# Revit family: Faucet_Bathroom-DXV-Equility-D3510940X_Series
name_source: partatom
category: Plumbing Fixtures
revit_build: Autodesk Revit 2014 (Build: 20130308_1515(x64)
units: mm (PartAtom-declared; Revit-internal decimal feet)

## types (9) — shared parameters
ADA Compliant = Yes
Assembly Code = D2010710
CW Connection = Yes
CWFU = 1.5
Cold Water Connection Diameter = 1/2"
Cold Water Connection Radius = 1/4"
Default Elevation = 40"
Description = Equility Wall Mount Faucet
HW Connection = Yes
HWFU = 1.5
Height = 3 3/8"
Hot Water Connection Diameter = 1"
Hot Water Connection Radius = 1/4"
Installation Type = Wall Mounted
Length = 9"
Manufacturer = DXV
Price = Prices may vary. Please consult Manufacturer Representative for most up-to-date price list.
Product Documentation Link = https://dxv01.blob.core.windows.net
Revised Date = 12/05/2018
URL = http://www.dxv.com
Vent Connection = No
WFU = 2
Warranty Documentation Link = https://www.dxv.com
Waste Connection = No
Width = 3"

## per-type parameters (varying)
| type | Finish | Flow Rate | Material | Product Page URL |
| D35109400.100 | Metal-DXV-100-Polished Chrome | 1.5 GPM (5.7L/min) | Metal-DXV-100-Polished Chrome | http://www.dxv.com |
| D35109400.144 | Metal-DXV-144-Brushed Nickel | 1.5 GPM (5.7L/min) | Metal-DXV-144-Brushed Nickel | http://www.dxv.com |
| D35109400.243 | Metal-DXV-243-Matte Black | 1.5 GPM (5.7L/min) | Metal-DXV-243-Matte Black | http://www.dxv.com |
| D3510940C.100 | Metal-DXV-100-Polished Chrome | 1.2 gpm (4.5 L/min) | Metal-DXV-100-Polished Chrome | https://www.dxv.com |
| D3510940C.144 | Metal-DXV-144-Brushed Nickel | 1.2 gpm (4.5 L/min) | Metal-DXV-144-Brushed Nickel | https://www.dxv.com |
| D3510940C.243 | Metal-DXV-243-Matte Black | 1.2 gpm (4.5 L/min) | Metal-DXV-243-Matte Black | https://www.dxv.com |
| D35109400RB.100 | Metal-DXV-100-Polished Chrome | 1.5 GPM (5.7L/min) | Metal-DXV-100-Polished Chrome | https://www.dxv.com |
| D35109400RB.144 | Metal-DXV-144-Brushed Nickel | 1.5 GPM (5.7L/min) | Metal-DXV-144-Brushed Nickel | https://www.dxv.com |
| D35109400RB.243 | Metal-DXV-243-Matte Black | 1.5 GPM (5.7L/min) | Metal-DXV-243-Matte Black | https://www.dxv.com |

note: column(s) folded — value = type name in every type: Model

## geometry (parser evidence)
native form markers: Sweep x3
no freeform markers — native parametric forms only
